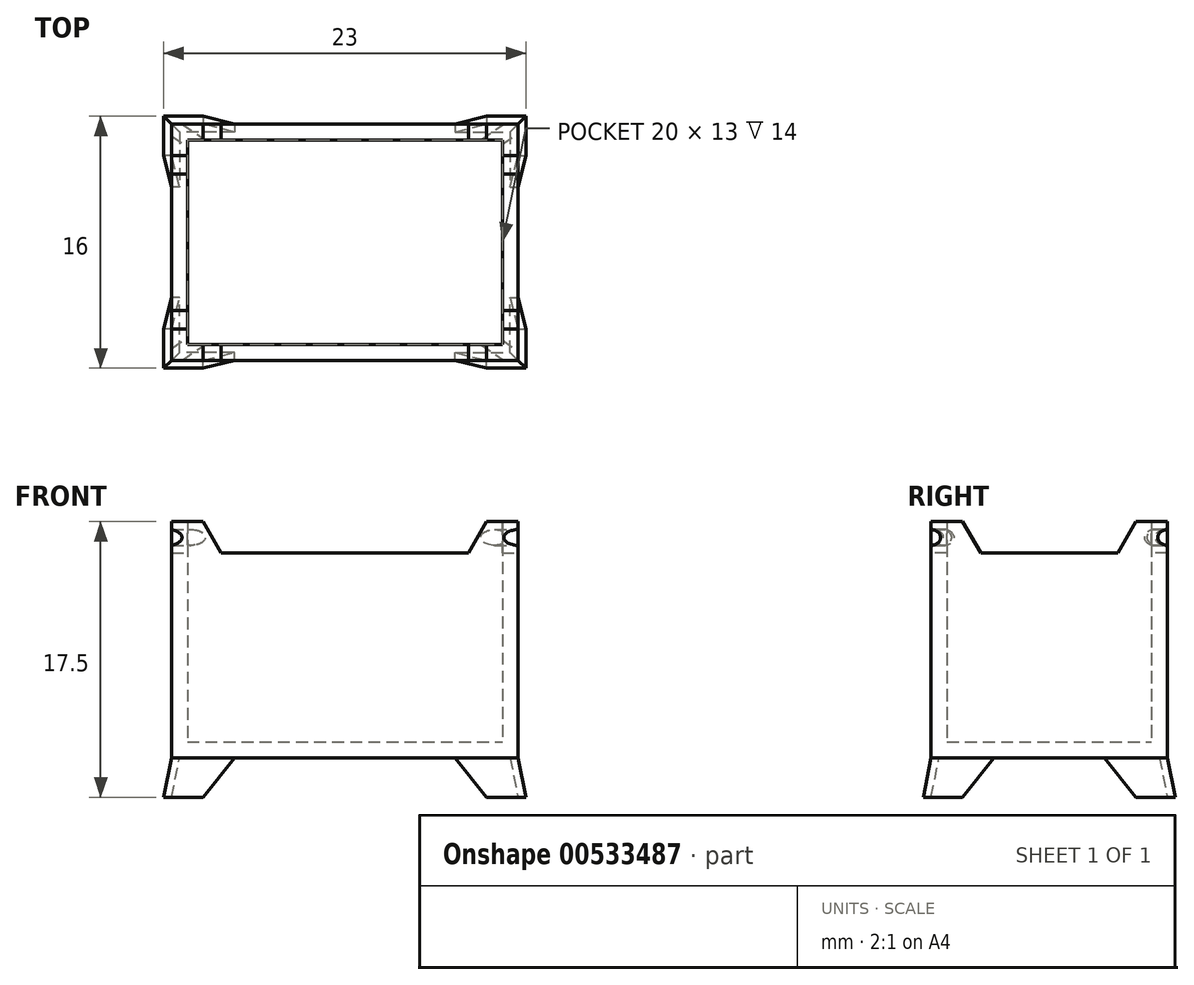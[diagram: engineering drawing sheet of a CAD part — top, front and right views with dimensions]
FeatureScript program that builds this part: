
annotation { "Feature Type Name" : "Feature", "Feature Type Description" : "" }
export const myFeature = defineFeature(function(context is Context, id is Id, definition is map)
    precondition{}
    {
        {
            var Q0;
            Q0=qCreatedBy(makeId("Top.planeOp"),FACE);
            var sketch = newSketch(context, id + "F0", { "sketchPlane" : qUnion([Q0])});
            skLineSegment(sketch, "E0.bottom", {"start": v(0, 0) * mm, "end": v(22, 0) * mm});
            skLineSegment(sketch, "E0.top", {"start": v(0, 15) * mm, "end": v(22, 15) * mm});
            skLineSegment(sketch, "E0.left", {"start": v(0, 0) * mm, "end": v(0, 15) * mm});
            skLineSegment(sketch, "E0.right", {"start": v(22, 0) * mm, "end": v(22, 15) * mm});
            skSolve(sketch);
        }
        {
            var Q0;
            Q0 = qSketchRegion(id + "F0", true);
            extrude(context, id + "F1", {"entities" : qUnion([Q0]), "depth" : 18 * mm, "offsetDistance" : 25 * mm});
        }
        {
            var Q0;
            Q0=makeQuery(id+"F1.opExtrude","CAP_FACE",FACE,{"disambiguationData":[OSD([sQuery(id+"F0.wireOp",EDGE,"E0.bottom"),sQuery(id+"F0.wireOp",EDGE,"E0.top"),sQuery(id+"F0.wireOp",EDGE,"E0.left"),sQuery(id+"F0.wireOp",EDGE,"E0.right")])],"isStart":false});
            shell(context, id + "F2", {"entities" : qUnion([Q0]), "thickness" : 1 * mm});
        }
        {
            var Q0;
            Q0=makeQuery(id+"F1.opExtrude","CAP_FACE",FACE,{"disambiguationData":[OSD([sQuery(id+"F0.wireOp",EDGE,"E0.bottom"),sQuery(id+"F0.wireOp",EDGE,"E0.top"),sQuery(id+"F0.wireOp",EDGE,"E0.left"),sQuery(id+"F0.wireOp",EDGE,"E0.right")])],"isStart":true});
            var sketch = newSketch(context, id + "F3", { "sketchPlane" : qUnion([Q0])});
            skLineSegment(sketch, "E1", {"start": v(0, 0) * mm, "end": v(4, 0) * mm});
            skLineSegment(sketch, "E2", {"start": v(4, 0) * mm, "end": v(4, -0.5) * mm});
            skLineSegment(sketch, "E3", {"start": v(4, -0.5) * mm, "end": v(0.5, -0.5) * mm});
            skLineSegment(sketch, "E4", {"start": v(0.5, -0.5) * mm, "end": v(0.5, -4) * mm});
            skLineSegment(sketch, "E5", {"start": v(0.5, -4) * mm, "end": v(0, -4) * mm});
            skLineSegment(sketch, "E6", {"start": v(0, -4) * mm, "end": v(0, 0) * mm});
            skLineSegment(sketch, "E7", {"start": v(11, 0) * mm, "end": v(11, 1.02) * mm, "construction": true});
            skLineSegment(sketch, "E8", {"start": v(0, -7.5) * mm, "end": v(-1.1, -7.5) * mm, "construction": true});
            skLineSegment(sketch, "E9.MirrorCS", {"start": v(18, -0.5) * mm, "end": v(21.5, -0.5) * mm});
            skLineSegment(sketch, "E10.MirrorCS", {"start": v(18, 0) * mm, "end": v(18, -0.5) * mm});
            skLineSegment(sketch, "E11.MirrorCS", {"start": v(22, 0) * mm, "end": v(18, 0) * mm});
            skLineSegment(sketch, "E12.MirrorCS", {"start": v(22, -4) * mm, "end": v(22, 0) * mm});
            skLineSegment(sketch, "E13.MirrorCS", {"start": v(21.5, -4) * mm, "end": v(22, -4) * mm});
            skLineSegment(sketch, "E14.MirrorCS", {"start": v(21.5, -0.5) * mm, "end": v(21.5, -4) * mm});
            skLineSegment(sketch, "E15.MirrorCS", {"start": v(0.5, -14.5) * mm, "end": v(0.5, -11) * mm});
            skLineSegment(sketch, "E16.MirrorCS", {"start": v(0.5, -11) * mm, "end": v(0, -11) * mm});
            skLineSegment(sketch, "E17.MirrorCS", {"start": v(0, -11) * mm, "end": v(0, -15) * mm});
            skLineSegment(sketch, "E18.MirrorCS", {"start": v(0, -15) * mm, "end": v(4, -15) * mm});
            skLineSegment(sketch, "E19.MirrorCS", {"start": v(4, -15) * mm, "end": v(4, -14.5) * mm});
            skLineSegment(sketch, "E20.MirrorCS", {"start": v(4, -14.5) * mm, "end": v(0.5, -14.5) * mm});
            skLineSegment(sketch, "E21.MirrorCS", {"start": v(22, -15) * mm, "end": v(18, -15) * mm});
            skLineSegment(sketch, "E22.MirrorCS", {"start": v(18, -15) * mm, "end": v(18, -14.5) * mm});
            skLineSegment(sketch, "E23.MirrorCS", {"start": v(18, -14.5) * mm, "end": v(21.5, -14.5) * mm});
            skLineSegment(sketch, "E24.MirrorCS", {"start": v(21.5, -14.5) * mm, "end": v(21.5, -11) * mm});
            skLineSegment(sketch, "E25.MirrorCS", {"start": v(21.5, -11) * mm, "end": v(22, -11) * mm});
            skLineSegment(sketch, "E26.MirrorCS", {"start": v(22, -11) * mm, "end": v(22, -15) * mm});
            skSolve(sketch);
        }
        {
            var Q0;
            Q0=qCreatedBy(makeId("Top.planeOp"),FACE);
            cPlane(context, id + "F4", {"entities" : qUnion([Q0]), "cplaneType" : CPlaneType.OFFSET, "offset" : 2.5 * mm, "oppositeDirection" : true, "width" : 150 * mm, "height" : 150 * mm});
        }
        {
            var Q0;
            Q0=qCreatedBy(id+"F4.planeOp",FACE);
            var sketch = newSketch(context, id + "F5", { "sketchPlane" : qUnion([Q0])});
            skPoint(sketch, "E27.0", {"position": v(22, 15) * mm});
            skLineSegment(sketch, "E28", {"start": v(11, 0) * mm, "end": v(11, -1.63) * mm, "construction": true});
            skPoint(sketch, "E28.endSnap0", {"position": v(11, 0) * mm});
            skLineSegment(sketch, "E29", {"start": v(0, 7.5) * mm, "end": v(-1.14, 7.5) * mm, "construction": true});
            skLineSegment(sketch, "E30", {"start": v(0, 0) * mm, "end": v(0, -0.5) * mm, "construction": true});
            skLineSegment(sketch, "E31", {"start": v(0, -0.5) * mm, "end": v(-0.5, -0.5) * mm, "construction": true});
            skLineSegment(sketch, "E32", {"start": v(22, 15) * mm, "end": v(22.5, 15) * mm, "construction": true});
            skLineSegment(sketch, "E33", {"start": v(22.5, 15) * mm, "end": v(22.5, 15.5) * mm, "construction": true});
            skLineSegment(sketch, "E34.bottom", {"start": v(-0.5, -0.5) * mm, "end": v(22.5, -0.5) * mm, "construction": true});
            skLineSegment(sketch, "E34.top", {"start": v(-0.5, 15.5) * mm, "end": v(22.5, 15.5) * mm, "construction": true});
            skLineSegment(sketch, "E34.left", {"start": v(-0.5, -0.5) * mm, "end": v(-0.5, 15.5) * mm, "construction": true});
            skLineSegment(sketch, "E34.right", {"start": v(22.5, -0.5) * mm, "end": v(22.5, 15.5) * mm, "construction": true});
            skLineSegment(sketch, "E35", {"start": v(-0.5, -0.5) * mm, "end": v(2, -0.5) * mm});
            skLineSegment(sketch, "E36", {"start": v(2, -0.5) * mm, "end": v(2, 0) * mm});
            skLineSegment(sketch, "E37", {"start": v(2, 0) * mm, "end": v(0, 0) * mm});
            skLineSegment(sketch, "E38", {"start": v(0, 0) * mm, "end": v(0, 2) * mm});
            skLineSegment(sketch, "E39", {"start": v(0, 2) * mm, "end": v(-0.5, 2) * mm});
            skLineSegment(sketch, "E40", {"start": v(-0.5, 2) * mm, "end": v(-0.5, -0.5) * mm});
            skLineSegment(sketch, "E41.MirrorCS", {"start": v(22, 0) * mm, "end": v(22, 2) * mm});
            skLineSegment(sketch, "E42.MirrorCS", {"start": v(22, 2) * mm, "end": v(22.5, 2) * mm});
            skLineSegment(sketch, "E43.MirrorCS", {"start": v(20, 0) * mm, "end": v(22, 0) * mm});
            skLineSegment(sketch, "E44.MirrorCS", {"start": v(20, -0.5) * mm, "end": v(20, 0) * mm});
            skLineSegment(sketch, "E45.MirrorCS", {"start": v(22, 7.5) * mm, "end": v(23.14, 7.5) * mm, "construction": true});
            skLineSegment(sketch, "E46.MirrorCS", {"start": v(0, 13) * mm, "end": v(-0.5, 13) * mm});
            skLineSegment(sketch, "E47.MirrorCS", {"start": v(0, 15) * mm, "end": v(0, 13) * mm});
            skLineSegment(sketch, "E48.MirrorCS", {"start": v(2, 15) * mm, "end": v(0, 15) * mm});
            skLineSegment(sketch, "E49.MirrorCS", {"start": v(2, 15.5) * mm, "end": v(2, 15) * mm});
            skLineSegment(sketch, "E50.MirrorCS", {"start": v(20, 15) * mm, "end": v(22, 15) * mm});
            skLineSegment(sketch, "E51.MirrorCS", {"start": v(20, 15.5) * mm, "end": v(20, 15) * mm});
            skLineSegment(sketch, "E52.MirrorCS", {"start": v(22, 13) * mm, "end": v(22.5, 13) * mm});
            skLineSegment(sketch, "E53", {"start": v(20, -0.5) * mm, "end": v(22.5, -0.5) * mm});
            skLineSegment(sketch, "E54", {"start": v(22.5, 2) * mm, "end": v(22.5, -0.5) * mm});
            skLineSegment(sketch, "E55", {"start": v(22, 15) * mm, "end": v(22, 13) * mm});
            skLineSegment(sketch, "E56", {"start": v(22.5, 13) * mm, "end": v(22.5, 15.5) * mm});
            skLineSegment(sketch, "E57", {"start": v(20, 15.5) * mm, "end": v(22.5, 15.5) * mm});
            skLineSegment(sketch, "E58", {"start": v(-0.5, 13) * mm, "end": v(-0.5, 15.5) * mm});
            skLineSegment(sketch, "E59", {"start": v(2, 15.5) * mm, "end": v(-0.5, 15.5) * mm});
            skSolve(sketch);
        }
        {
            var Q1;
            Q1=makeQuery(id+"F5.imprint","IMPRINT",FACE,{"disambiguationData":[TD([[makeQuery(id+"F5.imprint","IMPRINT",EDGE,{"derivedFrom":sQuery(id+"F5.wireOp",EDGE,"E35")}),1.0]])]});
            var Q2;
            Q2=makeQuery(id+"F3.imprint","IMPRINT",FACE,{"disambiguationData":[TD([[makeQuery(id+"F3.imprint","IMPRINT",EDGE,{"derivedFrom":sQuery(id+"F3.wireOp",EDGE,"E1")}),-1.0]])]});
            loft(context, id + "F6", {"operationType" : NewBodyOperationType.ADD, "sheetProfilesArray" : [{ "sheetProfileEntities" : qUnion([Q1]) }, { "sheetProfileEntities" : qUnion([Q2]) }]});
        }
        {
            var Q1;
            Q1=makeQuery(id+"F3.imprint","IMPRINT",FACE,{"disambiguationData":[TD([[makeQuery(id+"F3.imprint","IMPRINT",EDGE,{"derivedFrom":sQuery(id+"F3.wireOp",EDGE,"E15.MirrorCS")}),1.0]])]});
            var Q2;
            Q2=makeQuery(id+"F5.imprint","IMPRINT",FACE,{"disambiguationData":[TD([[makeQuery(id+"F5.imprint","IMPRINT",EDGE,{"derivedFrom":sQuery(id+"F5.wireOp",EDGE,"E46.MirrorCS")}),-1.0]])]});
            loft(context, id + "F7", {"operationType" : NewBodyOperationType.ADD, "sheetProfilesArray" : [{ "sheetProfileEntities" : qUnion([Q1]) }, { "sheetProfileEntities" : qUnion([Q2]) }]});
        }
        {
            var Q1;
            Q1=makeQuery(id+"F3.imprint","IMPRINT",FACE,{"disambiguationData":[TD([[makeQuery(id+"F3.imprint","IMPRINT",EDGE,{"derivedFrom":sQuery(id+"F3.wireOp",EDGE,"E22.MirrorCS")}),-1.0]])]});
            var Q2;
            Q2=makeQuery(id+"F5.imprint","IMPRINT",FACE,{"disambiguationData":[TD([[makeQuery(id+"F5.imprint","IMPRINT",EDGE,{"derivedFrom":sQuery(id+"F5.wireOp",EDGE,"E50.MirrorCS")}),1.0]])]});
            loft(context, id + "F8", {"operationType" : NewBodyOperationType.ADD, "sheetProfilesArray" : [{ "sheetProfileEntities" : qUnion([Q1]) }, { "sheetProfileEntities" : qUnion([Q2]) }]});
        }
        {
            var Q1;
            Q1=makeQuery(id+"F3.imprint","IMPRINT",FACE,{"disambiguationData":[TD([[makeQuery(id+"F3.imprint","IMPRINT",EDGE,{"derivedFrom":sQuery(id+"F3.wireOp",EDGE,"E9.MirrorCS")}),1.0]])]});
            var Q2;
            Q2=makeQuery(id+"F5.imprint","IMPRINT",FACE,{"disambiguationData":[TD([[makeQuery(id+"F5.imprint","IMPRINT",EDGE,{"derivedFrom":sQuery(id+"F5.wireOp",EDGE,"E42.MirrorCS")}),-1.0]])]});
            loft(context, id + "F9", {"operationType" : NewBodyOperationType.ADD, "sheetProfilesArray" : [{ "sheetProfileEntities" : qUnion([Q1]) }, { "sheetProfileEntities" : qUnion([Q2]) }]});
        }
        {
            var Q0;
            Q0=makeQuery(id+"F1.opExtrude","SWEPT_FACE",FACE,{"disambiguationData":[OSD([sQuery(id+"F0.wireOp",EDGE,"E0.bottom")])]});
            var sketch = newSketch(context, id + "F10", { "sketchPlane" : qUnion([Q0])});
            skLineSegment(sketch, "E60", {"start": v(22, 0) * mm, "end": v(22, 15) * mm, "construction": true});
            skLineSegment(sketch, "E61", {"start": v(22, 15) * mm, "end": v(20, 15) * mm});
            skLineSegment(sketch, "E62", {"start": v(20, 15) * mm, "end": v(18.85, 13) * mm});
            skLineSegment(sketch, "E63", {"start": v(18.85, 13) * mm, "end": v(3.15, 13) * mm});
            skLineSegment(sketch, "E64", {"start": v(3.15, 13) * mm, "end": v(2, 15) * mm});
            skLineSegment(sketch, "E65", {"start": v(2, 15) * mm, "end": v(0, 15) * mm});
            skSolve(sketch);
        }
        {
            var Q0;
            Q0 = qSketchRegion(id + "F10", true);
            var Q1;
            {var subQ0=sQuery(id+"F10.wireOp",EDGE,"E61");Q1=makeQuery(id+"F10.imprint","IMPRINT",FACE,{"disambiguationData":[TD([[makeQuery(id+"F10.imprint","IMPRINT",EDGE,{"derivedFrom":subQ0}),-1.0]])]});}
            extrude(context, id + "F11", {"entities" : qUnion([Q0, Q1]), "operationType" : NewBodyOperationType.REMOVE, "oppositeDirection" : true, "depth" : 25 * mm, "offsetDistance" : 25 * mm});
        }
        {
            var Q0;
            Q0=makeQuery(id+"F1.opExtrude","SWEPT_FACE",FACE,{"disambiguationData":[OSD([sQuery(id+"F0.wireOp",EDGE,"E0.right")])]});
            var sketch = newSketch(context, id + "F12", { "sketchPlane" : qUnion([Q0])});
            skLineSegment(sketch, "E66", {"start": v(0, 15) * mm, "end": v(2, 15) * mm});
            skLineSegment(sketch, "E67", {"start": v(2, 15) * mm, "end": v(3.15, 13) * mm});
            skLineSegment(sketch, "E68", {"start": v(3.15, 13) * mm, "end": v(11.85, 13) * mm});
            skLineSegment(sketch, "E69", {"start": v(11.85, 13) * mm, "end": v(13, 15) * mm});
            skLineSegment(sketch, "E70", {"start": v(13, 15) * mm, "end": v(15, 15) * mm});
            skSolve(sketch);
        }
        {
            var Q0;
            Q0 = qSketchRegion(id + "F12", true);
            var Q1;
            {var subQ0=sQuery(id+"F12.wireOp",EDGE,"E67");Q1=makeQuery(id+"F12.imprint","IMPRINT",FACE,{"disambiguationData":[TD([[makeQuery(id+"F12.imprint","IMPRINT",EDGE,{"derivedFrom":subQ0}),1.0]])]});}
            extrude(context, id + "F13", {"entities" : qUnion([Q0, Q1]), "operationType" : NewBodyOperationType.REMOVE, "oppositeDirection" : true, "depth" : 25 * mm, "offsetDistance" : 25 * mm});
        }
        {
            var Q0;
            Q0=makeQuery(id+"F1.opExtrude","SWEPT_FACE",FACE,{"disambiguationData":[OSD([sQuery(id+"F0.wireOp",EDGE,"E0.right")])]});
            var sketch = newSketch(context, id + "F14", { "sketchPlane" : qUnion([Q0])});
            skCircle(sketch, "E71", {"center": v(13.71, 14) * mm, "radius": 0.5 * mm});
            skPoint(sketch, "E71.centerSnap0", {"position": v(12.42, 14) * mm});
            skLineSegment(sketch, "E72", {"start": v(7.5, 13) * mm, "end": v(7.5, 13.6) * mm, "construction": true});
            skCircle(sketch, "E73.MirrorC", {"center": v(1.29, 14) * mm, "radius": 0.5 * mm});
            skLineSegment(sketch, "E74", {"start": v(12.42, 14) * mm, "end": v(15, 14) * mm, "construction": true});
            skSolve(sketch);
        }
        {
            var Q0;
            Q0=makeQuery(id+"F1.opExtrude","SWEPT_EDGE",EDGE,{"disambiguationData":[OSD([sQuery(id+"F0.wireOp",EDGE,"E0.top"),sQuery(id+"F0.wireOp",EDGE,"E0.right")])]});
            cPlane(context, id + "F15", {"entities" : qUnion([Q0]), "cplaneType" : CPlaneType.LINE_ANGLE, "offset" : 25 * mm, "angle" : 146 * degree, "width" : 150 * mm, "height" : 150 * mm});
        }
        {
            var Q0;
            Q0=qCreatedBy(id+"F15.planeOp",FACE);
            var sketch = newSketch(context, id + "F16", { "sketchPlane" : qUnion([Q0])});
            skPoint(sketch, "E75.0", {"position": v(0.13, 14) * mm});
            skCircle(sketch, "E76", {"center": v(0.13, 14) * mm, "radius": 0.5 * mm});
            skSolve(sketch);
        }
        {
            var Q0;
            Q0 = qSketchRegion(id + "F16", true);
            extrude(context, id + "F17", {"entities" : qUnion([Q0]), "operationType" : NewBodyOperationType.REMOVE, "oppositeDirection" : true, "depth" : 50 * mm, "offsetDistance" : 25 * mm});
        }
        {
            var Q0;
            Q0=makeQuery(id+"F1.opExtrude","SWEPT_EDGE",EDGE,{"disambiguationData":[OSD([sQuery(id+"F0.wireOp",EDGE,"E0.bottom"),sQuery(id+"F0.wireOp",EDGE,"E0.right")])]});
            cPlane(context, id + "F18", {"entities" : qUnion([Q0]), "cplaneType" : CPlaneType.LINE_ANGLE, "offset" : 25 * mm, "angle" : 146 * degree, "oppositeDirection" : true, "width" : 150 * mm, "height" : 150 * mm});
        }
        {
            var Q0;
            Q0=qCreatedBy(id+"F18.planeOp",FACE);
            var sketch = newSketch(context, id + "F19", { "sketchPlane" : qUnion([Q0])});
            skLineSegment(sketch, "E77.0", {"start": v(12.3, 15) * mm, "end": v(12.3, 0) * mm});
            skLineSegment(sketch, "E78", {"start": v(12.3, 15) * mm, "end": v(12.3, 14) * mm, "construction": true});
            skCircle(sketch, "E79", {"center": v(12.3, 14) * mm, "radius": 0.5 * mm});
            skSolve(sketch);
        }
        {
            var Q0;
            Q0 = qSketchRegion(id + "F19", true);
            extrude(context, id + "F20", {"entities" : qUnion([Q0]), "operationType" : NewBodyOperationType.REMOVE, "oppositeDirection" : true, "depth" : 50 * mm, "offsetDistance" : 25 * mm});
        }
    });
